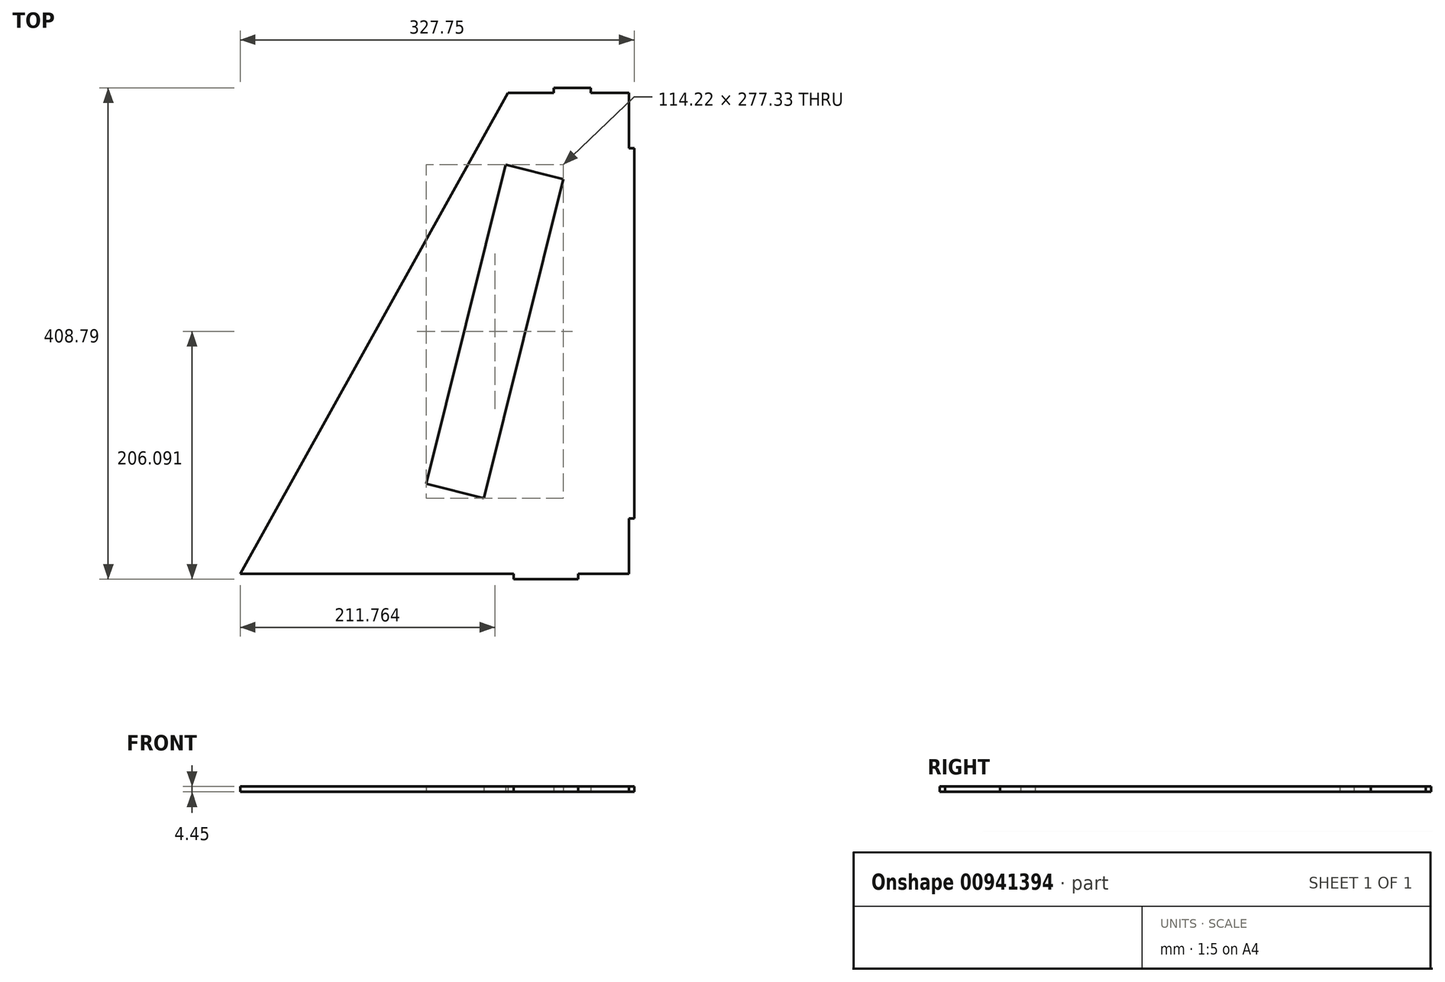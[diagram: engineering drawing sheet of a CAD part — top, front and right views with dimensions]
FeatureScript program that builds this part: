
annotation { "Feature Type Name" : "Feature", "Feature Type Description" : "" }
export const myFeature = defineFeature(function(context is Context, id is Id, definition is map)
    precondition{}
    {
        {
            var Q0;
            Q0=qCreatedBy(makeId("Top.planeOp"),FACE);
            var sketch = newSketch(context, id + "F0", { "sketchPlane" : qUnion([Q0])});
            skLineSegment(sketch, "E0.bottom", {"start": v(50.27, -200) * mm, "end": v(8.2, -200) * mm});
            skLineSegment(sketch, "E0.top", {"start": v(50.27, 200) * mm, "end": v(19.65, 200) * mm});
            skLineSegment(sketch, "E0.left", {"start": v(50.27, -200) * mm, "end": v(50.27, -154.1) * mm});
            skPoint(sketch, "E0.middle", {"position": v(0, 0) * mm});
            skLineSegment(sketch, "E1", {"start": v(-101.13, -200) * mm, "end": v(-50.27, -200) * mm});
            skPoint(sketch, "E2.middle", {"position": v(-20.63, 11.2) * mm});
            skLineSegment(sketch, "E3", {"start": v(-4.15, 128.33) * mm, "end": v(-70.45, -137.02) * mm});
            skLineSegment(sketch, "E4", {"start": v(-70.45, -137.02) * mm, "end": v(-118.38, -125.05) * mm});
            skLineSegment(sketch, "E5", {"start": v(-4.15, 128.33) * mm, "end": v(-52.08, 140.3) * mm});
            skLineSegment(sketch, "E6", {"start": v(-52.08, 140.3) * mm, "end": v(-118.38, -125.05) * mm});
            skLineSegment(sketch, "E7.top", {"start": v(18.65, 204.34) * mm, "end": v(-12.11, 204.34) * mm});
            skLineSegment(sketch, "E8.trimOffspring", {"start": v(19.65, 200) * mm, "end": v(18.65, 204.34) * mm});
            skLineSegment(sketch, "E9.trimOffspring", {"start": v(-19.65, 200) * mm, "end": v(-50.27, 200) * mm});
            skPoint(sketch, "E7.right.start.orphan", {"position": v(-18.65, -204.34) * mm});
            skPoint(sketch, "E7.left.start.orphan", {"position": v(12.11, -204.34) * mm});
            skLineSegment(sketch, "E10.bottom", {"start": v(54.72, -154.1) * mm, "end": v(50.27, -154.1) * mm});
            skLineSegment(sketch, "E10.top", {"start": v(54.72, 154.1) * mm, "end": v(50.27, 154.1) * mm});
            skLineSegment(sketch, "E10.left", {"start": v(54.72, -154.1) * mm, "end": v(54.72, 154.1) * mm});
            skPoint(sketch, "E10.middle", {"position": v(50.27, 0) * mm});
            skPoint(sketch, "E10.right.end.orphan", {"position": v(45.82, 154.1) * mm});
            skPoint(sketch, "E11.orphan", {"position": v(45.82, -154.1) * mm});
            skLineSegment(sketch, "E12.trimOffspring", {"start": v(50.27, 154.1) * mm, "end": v(50.27, 200) * mm});
            skLineSegment(sketch, "E13.bottom", {"start": v(8.2, -204.45) * mm, "end": v(-45.51, -204.45) * mm});
            skLineSegment(sketch, "E13.left", {"start": v(8.2, -204.45) * mm, "end": v(8.2, -200) * mm});
            skLineSegment(sketch, "E13.right", {"start": v(-45.51, -204.45) * mm, "end": v(-45.5, -200) * mm});
            skPoint(sketch, "E13.middle", {"position": v(-18.65, -200) * mm});
            skLineSegment(sketch, "E14.trimOffspring", {"start": v(-45.5, -200) * mm, "end": v(-50.27, -200) * mm});
            skPoint(sketch, "E13.top.end.orphan", {"position": v(-45.49, -195.55) * mm});
            skPoint(sketch, "E13.top.start.orphan", {"position": v(8.22, -195.55) * mm});
            skLineSegment(sketch, "E15", {"start": v(-19.65, 200) * mm, "end": v(-12.11, 200) * mm});
            skLineSegment(sketch, "E16", {"start": v(-12.11, 200) * mm, "end": v(-12.11, 204.34) * mm});
            skLineSegment(sketch, "E17", {"start": v(-101.13, -200) * mm, "end": v(-273.03, -200) * mm});
            skLineSegment(sketch, "E18", {"start": v(-273.03, -200) * mm, "end": v(-50.27, 200) * mm});
            skLineSegment(sketch, "E19", {"start": v(18.65, 204.34) * mm, "end": v(18.65, 200) * mm});
            skLineSegment(sketch, "E20", {"start": v(18.65, 200) * mm, "end": v(19.65, 200) * mm});
            skSolve(sketch);
        }
        {
            var Q0;
            Q0=makeQuery(id+"F0.imprint","IMPRINT",FACE,{"disambiguationData":[TD([[makeQuery(id+"F0.imprint","IMPRINT",EDGE,{"derivedFrom":sQuery(id+"F0.wireOp",EDGE,"E0.bottom")}),-1.0]])]});
            extrude(context, id + "F1", {"entities" : qUnion([Q0]), "depth" : 4.45 * mm, "offsetDistance" : 25 * mm});
        }
    });
